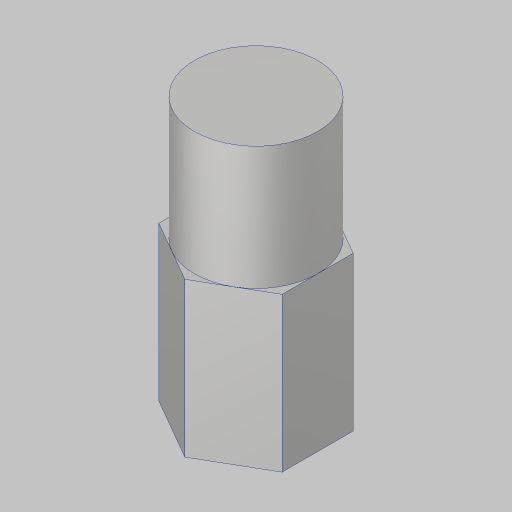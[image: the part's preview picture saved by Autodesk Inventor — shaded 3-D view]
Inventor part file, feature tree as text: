
AUTODESK INVENTOR PART (.ipt)
format: ipt  version: 2023.5 (Build 275446000, 446)  size: 116,736 bytes
history: native  units: in
note: dims shown in document units (in); Inventor stores cm internally (conversion verified against a paired STEP export)
features: extrude x2, sketch x2, thread x1, projected_geometry x1
ambient origin geometry x8: Origin, YZ Plane, XZ Plane, XY Plane, X Axis, Y Axis, Z Axis, Center Point
bodies: Solid1 (feature_tree)
feature tree (6):
  extrude  "Extrusion1"  Depth=1.125in TaperAngle=0.0deg
  extrude  "Extrusion2"  Depth=0.5in TaperAngle=0.0deg
  thread  "Thread1"  [1 undecoded]
  sketch  "Sketch1"  dims[d0=0.5in d1=1.125in d2=0.0in]
  sketch  "Sketch2"  dims[d3=0.5in d4=0.5in d5=0.0in d6=0.5in d7=0.0in]
  projected_geometry  "Projected Loop1"
note: 1 required parameter value undecoded (feature->parameter linkage not recoverable at this tier; creation-order binding heuristic only, values carry confidence <= 0.55)
